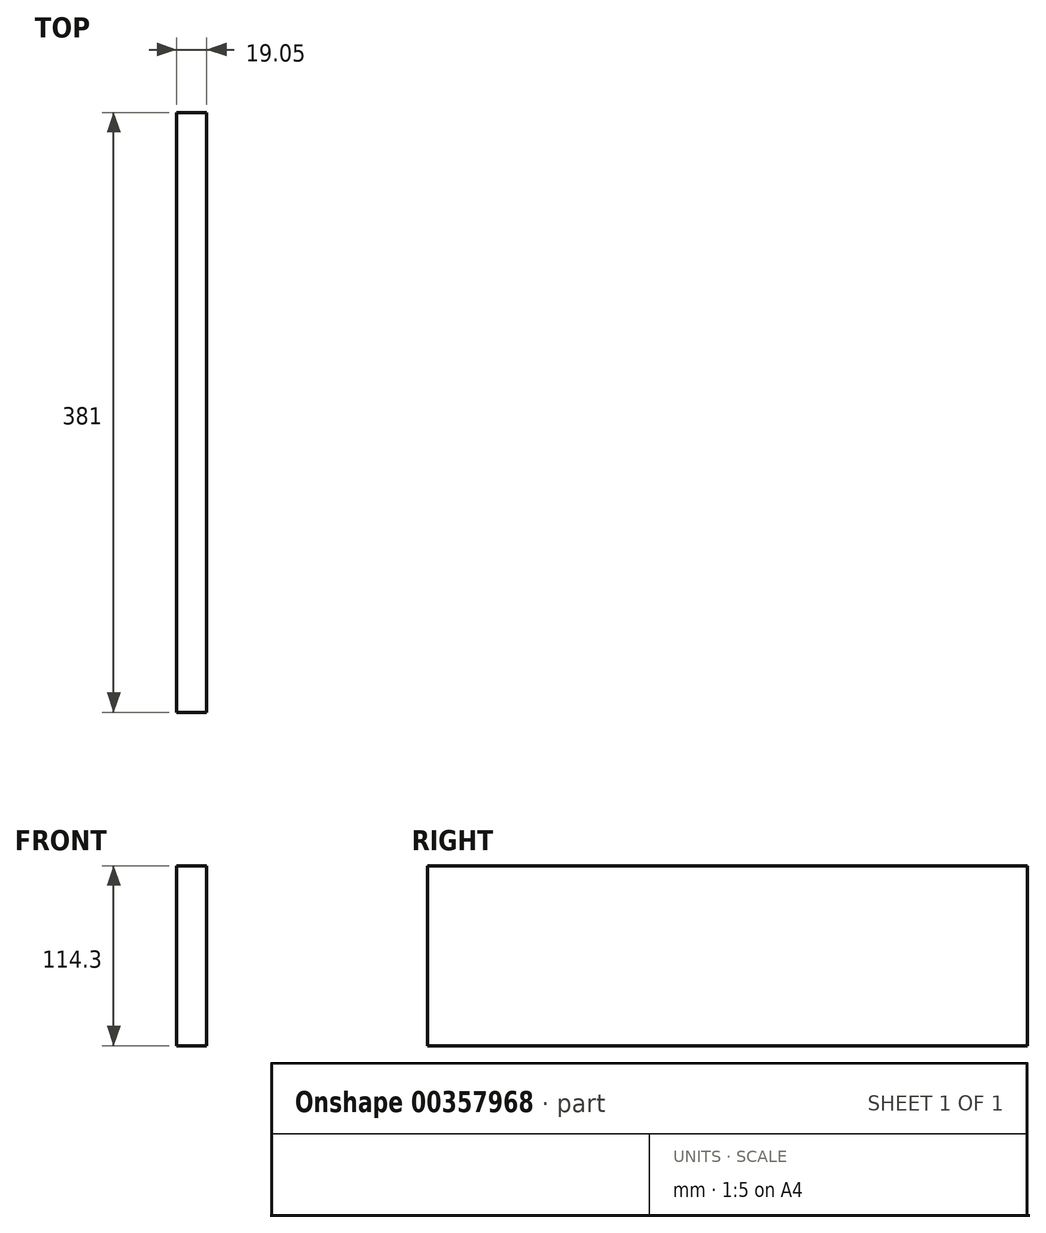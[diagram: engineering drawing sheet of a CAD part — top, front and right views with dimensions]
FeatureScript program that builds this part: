
annotation { "Feature Type Name" : "Feature", "Feature Type Description" : "" }
export const myFeature = defineFeature(function(context is Context, id is Id, definition is map)
    precondition{}
    {
        {
            var Q0;
            Q0=qCreatedBy(makeId("Right.planeOp"),FACE);
            var sketch = newSketch(context, id + "F0", { "sketchPlane" : qUnion([Q0])});
            skLineSegment(sketch, "E0.bottom", {"start": v(190.5, -57.15) * mm, "end": v(-190.5, -57.15) * mm});
            skLineSegment(sketch, "E0.top", {"start": v(190.5, 57.15) * mm, "end": v(-190.5, 57.15) * mm});
            skLineSegment(sketch, "E0.left", {"start": v(190.5, -57.15) * mm, "end": v(190.5, 57.15) * mm});
            skLineSegment(sketch, "E0.right", {"start": v(-190.5, -57.15) * mm, "end": v(-190.5, 57.15) * mm});
            skPoint(sketch, "E0.middle", {"position": v(0, 0) * mm});
            skSolve(sketch);
        }
        {
            var Q0;
            Q0=makeQuery(id+"F0.imprint","IMPRINT",FACE,{"disambiguationData":[TD([[makeQuery(id+"F0.imprint","IMPRINT",EDGE,{"derivedFrom":sQuery(id+"F0.wireOp",EDGE,"E0.bottom")}),-1.0]])]});
            extrude(context, id + "F1", {"entities" : qUnion([Q0]), "depth" : 19.05 * mm});
        }
    });
